# Revit family: Sink-Bathroom_Under_Mount-KOHLER-Thoreau-K-2907
name_source: partatom
category: Plumbing Fixtures
revit_build: Autodesk Revit 2015 (Build: 20140606_1530(x64)
units: mm (PartAtom-declared; Revit-internal decimal feet)

## types (6) — shared parameters
ADA Compliant = Yes
Assembly Code = D2010400
CW Connection = No
Cold Water Inlet = Cold Water Inlet
Date Modified = 12/29/2017
Default Elevation = 36"
HW Connection = No
Height = 8 5/8"
Hot Water Inlet = Hot Water Inlet
Length = 24"
Manufacturer = KOHLER Co.
MasterFormat 1995 = 15410
MasterFormat 2004 = 22.41.16
Material = Enameled Cast Iron
Product Documentation Link = http://www.us.kohler.com
Product Name = Thoreau
Product Page URL = http://www.us.kohler.com
URL = https://www.us.kohler.com
Vent Connection = No
Waste Connection = Yes
Waste Water Outlet = Waste Water Outlet
Width = 18"

## per-type parameters (varying)
| type | 4inch Hole | 8inch Hole | Description | Finish | Model | Type |
| 8" widespread faucet holes, 0-White | No | Yes | Under-mount bathroom sink with oversize 8inch widespread faucet holes | Kohler-Enameled_Cast_Iron-0-White | K-2907-8U-0 | 4 |
| 8" widespread faucet holes, 96-Biscuit | No | Yes | Under-mount bathroom sink with oversize 8inch widespread faucet holes | Kohler-Enameled_Cast_Iron-96-Biscuit | K-2907-8U-96 | 5 |
| 8" widespread faucet holes, 47-Almond | No | Yes | Under-mount bathroom sink with oversize 8inch widespread faucet holes | Kohler-Enameled_Cast_Iron-47-Almond | K-2907-8U-47 | 6 |
| 4" centerset faucet holes, 0-White | Yes | No | Under-mount bathroom sink with oversize 4inch centerset faucet holes | Kohler-Enameled_Cast_Iron-0-White | K-2907-4U-0 | 1 |
| 4" centerset faucet holes, 96-Biscuit | Yes | No | Under-mount bathroom sink with oversize 4inch centerset faucet holes | Kohler-Enameled_Cast_Iron-96-Biscuit | K-2907-4U-96 | 2 |
| 4" centerset faucet holes, 47-Almond | Yes | No | Under-mount bathroom sink with oversize 4inch centerset faucet holes | Kohler-Enameled_Cast_Iron-47-Almond | K-2907-4U-47 | 3 |

## geometry (parser evidence)
native form markers: Sweep x5
no freeform markers — native parametric forms only
